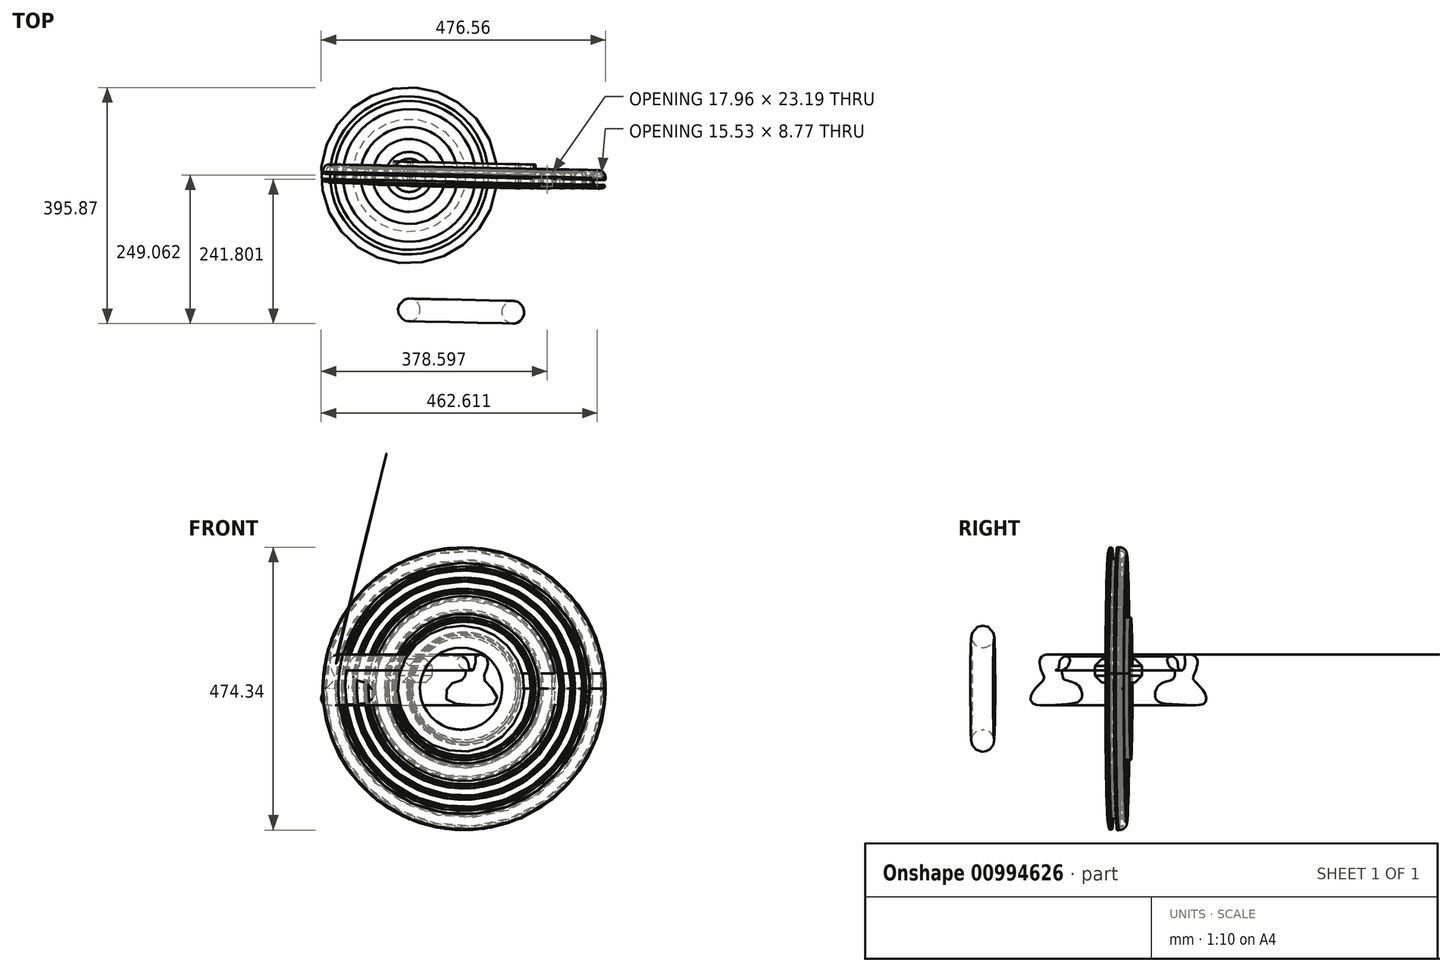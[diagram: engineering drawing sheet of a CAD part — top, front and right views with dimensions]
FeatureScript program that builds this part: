
annotation { "Feature Type Name" : "Feature", "Feature Type Description" : "" }
export const myFeature = defineFeature(function(context is Context, id is Id, definition is map)
    precondition{}
    {
        {
            var Q0;
            Q0=qCreatedBy(makeId("Front.planeOp"),FACE);
            var sketch = newSketch(context, id + "F0", { "sketchPlane" : qUnion([Q0])});
            skCircle(sketch, "E0.cCircle", {"center": v(-127.24, 29.71) * mm, "radius": 19.67 * mm, "construction": true});
            skLineSegment(sketch, "E0.0", {"start": v(-119.1, 10.05) * mm, "end": v(-135.39, 10.05) * mm});
            skLineSegment(sketch, "E0.1", {"start": v(-135.39, 10.05) * mm, "end": v(-146.9, 21.57) * mm});
            skLineSegment(sketch, "E0.2", {"start": v(-146.9, 21.57) * mm, "end": v(-146.9, 37.86) * mm});
            skLineSegment(sketch, "E0.3", {"start": v(-146.9, 37.86) * mm, "end": v(-135.39, 49.38) * mm});
            skLineSegment(sketch, "E0.4", {"start": v(-135.39, 49.38) * mm, "end": v(-119.1, 49.38) * mm});
            skLineSegment(sketch, "E0.5", {"start": v(-119.1, 49.38) * mm, "end": v(-107.57, 37.86) * mm});
            skLineSegment(sketch, "E0.6", {"start": v(-107.57, 37.86) * mm, "end": v(-107.57, 21.57) * mm});
            skLineSegment(sketch, "E0.7", {"start": v(-107.57, 21.57) * mm, "end": v(-119.1, 10.05) * mm});
            skPoint(sketch, "E0.0.midPoint", {"position": v(-127.24, 10.05) * mm});
            skSolve(sketch);
        }
        {
            var Q0;
            Q0=makeQuery(id+"F0.imprint","IMPRINT",FACE,{"disambiguationData":[TD([[makeQuery(id+"F0.imprint","IMPRINT",EDGE,{"derivedFrom":sQuery(id+"F0.wireOp",EDGE,"E0.0")}),-1.0]])]});
            var Q1;
            Q1=sQuery(id+"F0.wireOp",EDGE,"E0.6");
            revolve(context, id + "F1", {"surfaceOperationType" : NewSurfaceOperationType.NEW, "entities" : qUnion([Q0]), "axis" : qUnion([Q1]), "revolveType" : RevolveType.FULL});
        }
        {
            var Q0;
            Q0=qCreatedBy(makeId("Front.planeOp"),FACE);
            var sketch = newSketch(context, id + "F2", { "sketchPlane" : qUnion([Q0])});
            skFitSpline(sketch, "E1", {"points": [v(-13.85, 20.6) * mm, v(-13.25, 29.93) * mm, v(-20.47, 35.34) * mm, v(-25.58, 44.67) * mm, v(-25.88, 49.78) * mm, v(-21.37, 53.7) * mm, v(-16.55, 54) * mm, v(-12.95, 51.28) * mm, v(-9.94, 47.68) * mm, v(-8.13, 40.16) * mm, v(-7.23, 34.14) * mm, v(-3.92, 31.43) * mm, v(0, 31.13) * mm, v(3.9, 42.86) * mm, v(3.6, 53.09) * mm, v(6.3, 57) * mm, v(17.43, 55.8) * mm, v(22.55, 52.19) * mm, v(24.95, 43.76) * mm, v(23.45, 36.25) * mm, v(21.65, 29.33) * mm, v(17.43, 19.4) * mm, v(20.14, 12.18) * mm, v(36.99, -7.07) * mm, v(38.49, -22.4) * mm, v(25.25, -27.52) * mm, v(-14.75, -26.32) * mm, v(-44.23, -18.8) * mm, v(-43.93, 0) * mm, v(-32.2, 10.38) * mm, v(-15.95, 15.8) * mm, v(-13.85, 20.6) * mm]});
            skSolve(sketch);
        }
        {
            var Q0;
            Q0=makeQuery(id+"F2.imprint","IMPRINT",FACE,{"disambiguationData":[TD([[makeQuery(id+"F2.imprint","IMPRINT",EDGE,{"derivedFrom":sQuery(id+"F2.wireOp",EDGE,"E1")}),-1.0]])]});
            var Q1;
            Q1=makeQuery(id+"F1.opRevolve","SWEPT_EDGE",EDGE,{"disambiguationData":[OSD([sQuery(id+"F0.wireOp",EDGE,"E0.3"),sQuery(id+"F0.wireOp",EDGE,"E0.4")])]});
            revolve(context, id + "F3", {"surfaceOperationType" : NewSurfaceOperationType.NEW, "entities" : qUnion([Q0]), "axis" : qUnion([Q1]), "revolveType" : RevolveType.FULL});
        }
        {
            var Q0;
            Q0=qCreatedBy(makeId("Top.planeOp"),FACE);
            var sketch = newSketch(context, id + "F4", { "sketchPlane" : qUnion([Q0])});
            skText(sketch, "E2", { "text": "Home", "fontName": "OpenSans-Regular.ttf"});
            const initialGuessF4  = {"E2": [0.06589, -0.02145, 1, 0, 0.03995]};
            skSetInitialGuess(sketch, initialGuessF4);
            skSolve(sketch);
        }
        {
            var Q0;
            Q0 = qSketchRegion(id + "F4", true);
            extrude(context, id + "F5", {"entities" : qUnion([Q0]), "depth" : 25.4 * mm, "offsetDistance" : 25.4 * mm});
        }
        {
            var Q0;
            Q0=qCreatedBy(makeId("Top.planeOp"),FACE);
            var sketch = newSketch(context, id + "F6", { "sketchPlane" : qUnion([Q0])});
            skLineSegment(sketch, "E3", {"start": v(-11.92, 163.84) * mm, "end": v(-20.28, -218.05) * mm});
            skSolve(sketch);
        }
        {
            var Q0;
            Q0=makeQuery(id+"F5.opExtrude","SWEPT_FACE",FACE,{"disambiguationData":[OSD([sQuery(id+"F4.wireOp",EDGE,"E2.sketch_text.stroke-11")])]});
            var Q1;
            Q1=makeQuery(id+"F5.opExtrude","CAP_FACE",FACE,{"disambiguationData":[OSD([sQuery(id+"F4.wireOp",EDGE,"E2.sketch_text.stroke-0"),sQuery(id+"F4.wireOp",EDGE,"E2.sketch_text.stroke-1"),sQuery(id+"F4.wireOp",EDGE,"E2.sketch_text.stroke-2"),sQuery(id+"F4.wireOp",EDGE,"E2.sketch_text.stroke-3"),sQuery(id+"F4.wireOp",EDGE,"E2.sketch_text.stroke-4"),sQuery(id+"F4.wireOp",EDGE,"E2.sketch_text.stroke-5"),sQuery(id+"F4.wireOp",EDGE,"E2.sketch_text.stroke-6"),sQuery(id+"F4.wireOp",EDGE,"E2.sketch_text.stroke-7"),sQuery(id+"F4.wireOp",EDGE,"E2.sketch_text.stroke-8"),sQuery(id+"F4.wireOp",EDGE,"E2.sketch_text.stroke-9"),sQuery(id+"F4.wireOp",EDGE,"E2.sketch_text.stroke-10"),sQuery(id+"F4.wireOp",EDGE,"E2.sketch_text.stroke-11")])],"isStart":true});
            var Q2;
            Q2=makeQuery(id+"F5.opExtrude","CAP_FACE",FACE,{"disambiguationData":[OSD([sQuery(id+"F4.wireOp",EDGE,"E2.sketch_text.stroke-0"),sQuery(id+"F4.wireOp",EDGE,"E2.sketch_text.stroke-1"),sQuery(id+"F4.wireOp",EDGE,"E2.sketch_text.stroke-2"),sQuery(id+"F4.wireOp",EDGE,"E2.sketch_text.stroke-3"),sQuery(id+"F4.wireOp",EDGE,"E2.sketch_text.stroke-4"),sQuery(id+"F4.wireOp",EDGE,"E2.sketch_text.stroke-5"),sQuery(id+"F4.wireOp",EDGE,"E2.sketch_text.stroke-6"),sQuery(id+"F4.wireOp",EDGE,"E2.sketch_text.stroke-7"),sQuery(id+"F4.wireOp",EDGE,"E2.sketch_text.stroke-8"),sQuery(id+"F4.wireOp",EDGE,"E2.sketch_text.stroke-9"),sQuery(id+"F4.wireOp",EDGE,"E2.sketch_text.stroke-10"),sQuery(id+"F4.wireOp",EDGE,"E2.sketch_text.stroke-11")])],"isStart":false});
            var Q3;
            Q3=makeQuery(id+"F5.opExtrude","SWEPT_FACE",FACE,{"disambiguationData":[OSD([sQuery(id+"F4.wireOp",EDGE,"E2.sketch_text.stroke-1")])]});
            var Q4;
            Q4=makeQuery(id+"F5.opExtrude","SWEPT_FACE",FACE,{"disambiguationData":[OSD([sQuery(id+"F4.wireOp",EDGE,"E2.sketch_text.stroke-2")])]});
            var Q5;
            Q5=makeQuery(id+"F5.opExtrude","SWEPT_FACE",FACE,{"disambiguationData":[OSD([sQuery(id+"F4.wireOp",EDGE,"E2.sketch_text.stroke-6")])]});
            var Q6;
            Q6=makeQuery(id+"F5.opExtrude","SWEPT_FACE",FACE,{"disambiguationData":[OSD([sQuery(id+"F4.wireOp",EDGE,"E2.sketch_text.stroke-7")])]});
            var Q7;
            Q7=makeQuery(id+"F5.opExtrude","SWEPT_FACE",FACE,{"disambiguationData":[OSD([sQuery(id+"F4.wireOp",EDGE,"E2.sketch_text.stroke-8")])]});
            var Q8;
            Q8=makeQuery(id+"F5.opExtrude","SWEPT_FACE",FACE,{"disambiguationData":[OSD([sQuery(id+"F4.wireOp",EDGE,"E2.sketch_text.stroke-10")])]});
            var Q9;
            Q9=makeQuery(id+"F5.opExtrude","CAP_FACE",FACE,{"disambiguationData":[OSD([sQuery(id+"F4.wireOp",EDGE,"E2.sketch_text.stroke-12"),sQuery(id+"F4.wireOp",EDGE,"E2.sketch_text.stroke-13"),sQuery(id+"F4.wireOp",EDGE,"E2.sketch_text.stroke-14"),sQuery(id+"F4.wireOp",EDGE,"E2.sketch_text.stroke-15"),sQuery(id+"F4.wireOp",EDGE,"E2.sketch_text.stroke-16"),sQuery(id+"F4.wireOp",EDGE,"E2.sketch_text.stroke-17"),sQuery(id+"F4.wireOp",EDGE,"E2.sketch_text.stroke-18"),sQuery(id+"F4.wireOp",EDGE,"E2.sketch_text.stroke-19"),sQuery(id+"F4.wireOp",EDGE,"E2.sketch_text.stroke-20"),sQuery(id+"F4.wireOp",EDGE,"E2.sketch_text.stroke-21"),sQuery(id+"F4.wireOp",EDGE,"E2.sketch_text.stroke-22"),sQuery(id+"F4.wireOp",EDGE,"E2.sketch_text.stroke-23"),sQuery(id+"F4.wireOp",EDGE,"E2.sketch_text.stroke-24"),sQuery(id+"F4.wireOp",EDGE,"E2.sketch_text.stroke-25"),sQuery(id+"F4.wireOp",EDGE,"E2.sketch_text.stroke-26"),sQuery(id+"F4.wireOp",EDGE,"E2.sketch_text.stroke-27"),sQuery(id+"F4.wireOp",EDGE,"E2.sketch_text.stroke-28")])],"isStart":true});
            var Q10;
            Q10=makeQuery(id+"F5.opExtrude","CAP_FACE",FACE,{"disambiguationData":[OSD([sQuery(id+"F4.wireOp",EDGE,"E2.sketch_text.stroke-12"),sQuery(id+"F4.wireOp",EDGE,"E2.sketch_text.stroke-13"),sQuery(id+"F4.wireOp",EDGE,"E2.sketch_text.stroke-14"),sQuery(id+"F4.wireOp",EDGE,"E2.sketch_text.stroke-15"),sQuery(id+"F4.wireOp",EDGE,"E2.sketch_text.stroke-16"),sQuery(id+"F4.wireOp",EDGE,"E2.sketch_text.stroke-17"),sQuery(id+"F4.wireOp",EDGE,"E2.sketch_text.stroke-18"),sQuery(id+"F4.wireOp",EDGE,"E2.sketch_text.stroke-19"),sQuery(id+"F4.wireOp",EDGE,"E2.sketch_text.stroke-20"),sQuery(id+"F4.wireOp",EDGE,"E2.sketch_text.stroke-21"),sQuery(id+"F4.wireOp",EDGE,"E2.sketch_text.stroke-22"),sQuery(id+"F4.wireOp",EDGE,"E2.sketch_text.stroke-23"),sQuery(id+"F4.wireOp",EDGE,"E2.sketch_text.stroke-24"),sQuery(id+"F4.wireOp",EDGE,"E2.sketch_text.stroke-25"),sQuery(id+"F4.wireOp",EDGE,"E2.sketch_text.stroke-26"),sQuery(id+"F4.wireOp",EDGE,"E2.sketch_text.stroke-27"),sQuery(id+"F4.wireOp",EDGE,"E2.sketch_text.stroke-28")])],"isStart":false});
            var Q11;
            Q11=makeQuery(id+"F5.opExtrude","SWEPT_FACE",FACE,{"disambiguationData":[OSD([sQuery(id+"F4.wireOp",EDGE,"E2.sketch_text.stroke-41")])]});
            var Q12;
            Q12=makeQuery(id+"F5.opExtrude","SWEPT_FACE",FACE,{"disambiguationData":[OSD([sQuery(id+"F4.wireOp",EDGE,"E2.sketch_text.stroke-55")])]});
            var Q13;
            Q13=makeQuery(id+"F5.opExtrude","SWEPT_FACE",FACE,{"disambiguationData":[OSD([sQuery(id+"F4.wireOp",EDGE,"E2.sketch_text.stroke-29")])]});
            var Q14;
            Q14=makeQuery(id+"F5.opExtrude","CAP_FACE",FACE,{"disambiguationData":[OSD([sQuery(id+"F4.wireOp",EDGE,"E2.sketch_text.stroke-29"),sQuery(id+"F4.wireOp",EDGE,"E2.sketch_text.stroke-30"),sQuery(id+"F4.wireOp",EDGE,"E2.sketch_text.stroke-31"),sQuery(id+"F4.wireOp",EDGE,"E2.sketch_text.stroke-32"),sQuery(id+"F4.wireOp",EDGE,"E2.sketch_text.stroke-33"),sQuery(id+"F4.wireOp",EDGE,"E2.sketch_text.stroke-34"),sQuery(id+"F4.wireOp",EDGE,"E2.sketch_text.stroke-35"),sQuery(id+"F4.wireOp",EDGE,"E2.sketch_text.stroke-36"),sQuery(id+"F4.wireOp",EDGE,"E2.sketch_text.stroke-37"),sQuery(id+"F4.wireOp",EDGE,"E2.sketch_text.stroke-38"),sQuery(id+"F4.wireOp",EDGE,"E2.sketch_text.stroke-39"),sQuery(id+"F4.wireOp",EDGE,"E2.sketch_text.stroke-40"),sQuery(id+"F4.wireOp",EDGE,"E2.sketch_text.stroke-41"),sQuery(id+"F4.wireOp",EDGE,"E2.sketch_text.stroke-42"),sQuery(id+"F4.wireOp",EDGE,"E2.sketch_text.stroke-43"),sQuery(id+"F4.wireOp",EDGE,"E2.sketch_text.stroke-44"),sQuery(id+"F4.wireOp",EDGE,"E2.sketch_text.stroke-45"),sQuery(id+"F4.wireOp",EDGE,"E2.sketch_text.stroke-46"),sQuery(id+"F4.wireOp",EDGE,"E2.sketch_text.stroke-47"),sQuery(id+"F4.wireOp",EDGE,"E2.sketch_text.stroke-48"),sQuery(id+"F4.wireOp",EDGE,"E2.sketch_text.stroke-49"),sQuery(id+"F4.wireOp",EDGE,"E2.sketch_text.stroke-50"),sQuery(id+"F4.wireOp",EDGE,"E2.sketch_text.stroke-51"),sQuery(id+"F4.wireOp",EDGE,"E2.sketch_text.stroke-52"),sQuery(id+"F4.wireOp",EDGE,"E2.sketch_text.stroke-53"),sQuery(id+"F4.wireOp",EDGE,"E2.sketch_text.stroke-54"),sQuery(id+"F4.wireOp",EDGE,"E2.sketch_text.stroke-55"),sQuery(id+"F4.wireOp",EDGE,"E2.sketch_text.stroke-56")])],"isStart":true});
            var Q15;
            Q15=makeQuery(id+"F5.opExtrude","SWEPT_FACE",FACE,{"disambiguationData":[OSD([sQuery(id+"F4.wireOp",EDGE,"E2.sketch_text.stroke-44")])]});
            var Q16;
            Q16=makeQuery(id+"F5.opExtrude","CAP_FACE",FACE,{"disambiguationData":[OSD([sQuery(id+"F4.wireOp",EDGE,"E2.sketch_text.stroke-29"),sQuery(id+"F4.wireOp",EDGE,"E2.sketch_text.stroke-30"),sQuery(id+"F4.wireOp",EDGE,"E2.sketch_text.stroke-31"),sQuery(id+"F4.wireOp",EDGE,"E2.sketch_text.stroke-32"),sQuery(id+"F4.wireOp",EDGE,"E2.sketch_text.stroke-33"),sQuery(id+"F4.wireOp",EDGE,"E2.sketch_text.stroke-34"),sQuery(id+"F4.wireOp",EDGE,"E2.sketch_text.stroke-35"),sQuery(id+"F4.wireOp",EDGE,"E2.sketch_text.stroke-36"),sQuery(id+"F4.wireOp",EDGE,"E2.sketch_text.stroke-37"),sQuery(id+"F4.wireOp",EDGE,"E2.sketch_text.stroke-38"),sQuery(id+"F4.wireOp",EDGE,"E2.sketch_text.stroke-39"),sQuery(id+"F4.wireOp",EDGE,"E2.sketch_text.stroke-40"),sQuery(id+"F4.wireOp",EDGE,"E2.sketch_text.stroke-41"),sQuery(id+"F4.wireOp",EDGE,"E2.sketch_text.stroke-42"),sQuery(id+"F4.wireOp",EDGE,"E2.sketch_text.stroke-43"),sQuery(id+"F4.wireOp",EDGE,"E2.sketch_text.stroke-44"),sQuery(id+"F4.wireOp",EDGE,"E2.sketch_text.stroke-45"),sQuery(id+"F4.wireOp",EDGE,"E2.sketch_text.stroke-46"),sQuery(id+"F4.wireOp",EDGE,"E2.sketch_text.stroke-47"),sQuery(id+"F4.wireOp",EDGE,"E2.sketch_text.stroke-48"),sQuery(id+"F4.wireOp",EDGE,"E2.sketch_text.stroke-49"),sQuery(id+"F4.wireOp",EDGE,"E2.sketch_text.stroke-50"),sQuery(id+"F4.wireOp",EDGE,"E2.sketch_text.stroke-51"),sQuery(id+"F4.wireOp",EDGE,"E2.sketch_text.stroke-52"),sQuery(id+"F4.wireOp",EDGE,"E2.sketch_text.stroke-53"),sQuery(id+"F4.wireOp",EDGE,"E2.sketch_text.stroke-54"),sQuery(id+"F4.wireOp",EDGE,"E2.sketch_text.stroke-55"),sQuery(id+"F4.wireOp",EDGE,"E2.sketch_text.stroke-56")])],"isStart":false});
            var Q17;
            Q17=makeQuery(id+"F5.opExtrude","SWEPT_FACE",FACE,{"disambiguationData":[OSD([sQuery(id+"F4.wireOp",EDGE,"E2.sketch_text.stroke-45")])]});
            var Q18;
            Q18=makeQuery(id+"F5.opExtrude","SWEPT_FACE",FACE,{"disambiguationData":[OSD([sQuery(id+"F4.wireOp",EDGE,"E2.sketch_text.stroke-34")])]});
            var Q19;
            Q19=makeQuery(id+"F5.opExtrude","SWEPT_FACE",FACE,{"disambiguationData":[OSD([sQuery(id+"F4.wireOp",EDGE,"E2.sketch_text.stroke-36")])]});
            var Q20;
            Q20=makeQuery(id+"F5.opExtrude","CAP_FACE",FACE,{"disambiguationData":[OSD([sQuery(id+"F4.wireOp",EDGE,"E2.sketch_text.stroke-57"),sQuery(id+"F4.wireOp",EDGE,"E2.sketch_text.stroke-58"),sQuery(id+"F4.wireOp",EDGE,"E2.sketch_text.stroke-59"),sQuery(id+"F4.wireOp",EDGE,"E2.sketch_text.stroke-60"),sQuery(id+"F4.wireOp",EDGE,"E2.sketch_text.stroke-61"),sQuery(id+"F4.wireOp",EDGE,"E2.sketch_text.stroke-62"),sQuery(id+"F4.wireOp",EDGE,"E2.sketch_text.stroke-63"),sQuery(id+"F4.wireOp",EDGE,"E2.sketch_text.stroke-64"),sQuery(id+"F4.wireOp",EDGE,"E2.sketch_text.stroke-65"),sQuery(id+"F4.wireOp",EDGE,"E2.sketch_text.stroke-66"),sQuery(id+"F4.wireOp",EDGE,"E2.sketch_text.stroke-67"),sQuery(id+"F4.wireOp",EDGE,"E2.sketch_text.stroke-68"),sQuery(id+"F4.wireOp",EDGE,"E2.sketch_text.stroke-69"),sQuery(id+"F4.wireOp",EDGE,"E2.sketch_text.stroke-70"),sQuery(id+"F4.wireOp",EDGE,"E2.sketch_text.stroke-71"),sQuery(id+"F4.wireOp",EDGE,"E2.sketch_text.stroke-72"),sQuery(id+"F4.wireOp",EDGE,"E2.sketch_text.stroke-73"),sQuery(id+"F4.wireOp",EDGE,"E2.sketch_text.stroke-74"),sQuery(id+"F4.wireOp",EDGE,"E2.sketch_text.stroke-75")])],"isStart":true});
            var Q21;
            Q21=makeQuery(id+"F5.opExtrude","CAP_FACE",FACE,{"disambiguationData":[OSD([sQuery(id+"F4.wireOp",EDGE,"E2.sketch_text.stroke-57"),sQuery(id+"F4.wireOp",EDGE,"E2.sketch_text.stroke-58"),sQuery(id+"F4.wireOp",EDGE,"E2.sketch_text.stroke-59"),sQuery(id+"F4.wireOp",EDGE,"E2.sketch_text.stroke-60"),sQuery(id+"F4.wireOp",EDGE,"E2.sketch_text.stroke-61"),sQuery(id+"F4.wireOp",EDGE,"E2.sketch_text.stroke-62"),sQuery(id+"F4.wireOp",EDGE,"E2.sketch_text.stroke-63"),sQuery(id+"F4.wireOp",EDGE,"E2.sketch_text.stroke-64"),sQuery(id+"F4.wireOp",EDGE,"E2.sketch_text.stroke-65"),sQuery(id+"F4.wireOp",EDGE,"E2.sketch_text.stroke-66"),sQuery(id+"F4.wireOp",EDGE,"E2.sketch_text.stroke-67"),sQuery(id+"F4.wireOp",EDGE,"E2.sketch_text.stroke-68"),sQuery(id+"F4.wireOp",EDGE,"E2.sketch_text.stroke-69"),sQuery(id+"F4.wireOp",EDGE,"E2.sketch_text.stroke-70"),sQuery(id+"F4.wireOp",EDGE,"E2.sketch_text.stroke-71"),sQuery(id+"F4.wireOp",EDGE,"E2.sketch_text.stroke-72"),sQuery(id+"F4.wireOp",EDGE,"E2.sketch_text.stroke-73"),sQuery(id+"F4.wireOp",EDGE,"E2.sketch_text.stroke-74"),sQuery(id+"F4.wireOp",EDGE,"E2.sketch_text.stroke-75")])],"isStart":false});
            var Q22;
            Q22=makeQuery(id+"F5.opExtrude","SWEPT_FACE",FACE,{"disambiguationData":[OSD([sQuery(id+"F4.wireOp",EDGE,"E2.sketch_text.stroke-0")])]});
            var Q23;
            Q23=makeQuery(id+"F5.opExtrude","SWEPT_FACE",FACE,{"disambiguationData":[OSD([sQuery(id+"F4.wireOp",EDGE,"E2.sketch_text.stroke-3")])]});
            var Q24;
            Q24=makeQuery(id+"F5.opExtrude","SWEPT_FACE",FACE,{"disambiguationData":[OSD([sQuery(id+"F4.wireOp",EDGE,"E2.sketch_text.stroke-4")])]});
            var Q25;
            Q25=makeQuery(id+"F5.opExtrude","SWEPT_FACE",FACE,{"disambiguationData":[OSD([sQuery(id+"F4.wireOp",EDGE,"E2.sketch_text.stroke-5")])]});
            var Q26;
            Q26=makeQuery(id+"F5.opExtrude","SWEPT_FACE",FACE,{"disambiguationData":[OSD([sQuery(id+"F4.wireOp",EDGE,"E2.sketch_text.stroke-9")])]});
            var Q27;
            Q27=makeQuery(id+"F5.opExtrude","SWEPT_FACE",FACE,{"disambiguationData":[OSD([sQuery(id+"F4.wireOp",EDGE,"E2.sketch_text.stroke-56")])]});
            var Q28;
            Q28=makeQuery(id+"F5.opExtrude","SWEPT_FACE",FACE,{"disambiguationData":[OSD([sQuery(id+"F4.wireOp",EDGE,"E2.sketch_text.stroke-42")])]});
            var Q29;
            Q29=makeQuery(id+"F5.opExtrude","SWEPT_FACE",FACE,{"disambiguationData":[OSD([sQuery(id+"F4.wireOp",EDGE,"E2.sketch_text.stroke-43")])]});
            var Q30;
            Q30=makeQuery(id+"F5.opExtrude","SWEPT_FACE",FACE,{"disambiguationData":[OSD([sQuery(id+"F4.wireOp",EDGE,"E2.sketch_text.stroke-46")])]});
            var Q31;
            Q31=makeQuery(id+"F5.opExtrude","SWEPT_FACE",FACE,{"disambiguationData":[OSD([sQuery(id+"F4.wireOp",EDGE,"E2.sketch_text.stroke-50")])]});
            var Q32;
            Q32=makeQuery(id+"F5.opExtrude","SWEPT_FACE",FACE,{"disambiguationData":[OSD([sQuery(id+"F4.wireOp",EDGE,"E2.sketch_text.stroke-35")])]});
            var Q33;
            Q33=makeQuery(id+"F5.opExtrude","SWEPT_FACE",FACE,{"disambiguationData":[OSD([sQuery(id+"F4.wireOp",EDGE,"E2.sketch_text.stroke-73")])]});
            var Q34;
            Q34=makeQuery(id+"F5.opExtrude","SWEPT_FACE",FACE,{"disambiguationData":[OSD([sQuery(id+"F4.wireOp",EDGE,"E2.sketch_text.stroke-63")])]});
            var Q35;
            Q35=makeQuery(id+"F5.opExtrude","SWEPT_FACE",FACE,{"disambiguationData":[OSD([sQuery(id+"F4.wireOp",EDGE,"E2.sketch_text.stroke-64")])]});
            var Q36;
            Q36=makeQuery(id+"F5.opExtrude","SWEPT_FACE",FACE,{"disambiguationData":[OSD([sQuery(id+"F4.wireOp",EDGE,"E2.sketch_text.stroke-68")])]});
            var Q37;
            Q37=sQuery(id+"F6.wireOp",EDGE,"E3");
            revolve(context, id + "F7", {"surfaceOperationType" : NewSurfaceOperationType.NEW, "entities" : qUnion([Q0, Q1, Q2, Q3, Q4, Q5, Q6, Q7, Q8, Q9, Q10, Q11, Q12, Q13, Q14, Q15, Q16, Q17, Q18, Q19, Q20, Q21, Q22, Q23, Q24, Q25, Q26, Q27, Q28, Q29, Q30, Q31, Q32, Q33, Q34, Q35, Q36]), "axis" : qUnion([Q37]), "revolveType" : RevolveType.FULL});
        }
        {
            var Q0;
            Q0=qCreatedBy(makeId("Right.planeOp"),FACE);
            var sketch = newSketch(context, id + "F8", { "sketchPlane" : qUnion([Q0])});
            skCircle(sketch, "E4", {"center": v(-227.98, 84.73) * mm, "radius": 19 * mm});
            skSolve(sketch);
        }
        {
            var Q0;
            Q0=makeQuery(id+"F8.imprint","IMPRINT",FACE,{"disambiguationData":[TD([[makeQuery(id+"F8.imprint","IMPRINT",EDGE,{"derivedFrom":sQuery(id+"F8.wireOp",EDGE,"E4")}),1.0]])]});
            var Q1;
            {var subQ0=sQuery(id+"F4.wireOp",EDGE,"E2.sketch_text.stroke-69");var subQ1=sQuery(id+"F4.wireOp",EDGE,"E2.sketch_text.stroke-68");Q1=makeQuery(id+"F7.opRevolve","SWEPT_EDGE",EDGE,{"disambiguationData":[OSD([subQ1,subQ0]),TDD([makeQuery(id+"F5.opExtrude","CAP_VERTEX",VERTEX,{"disambiguationData":[OSD([subQ1,subQ0])],"isStart":false})]),OD(1.0)]});}
            sweep(context, id + "F9", {"profiles" : qUnion([Q0]), "path" : qUnion([Q1])});
        }
    });
